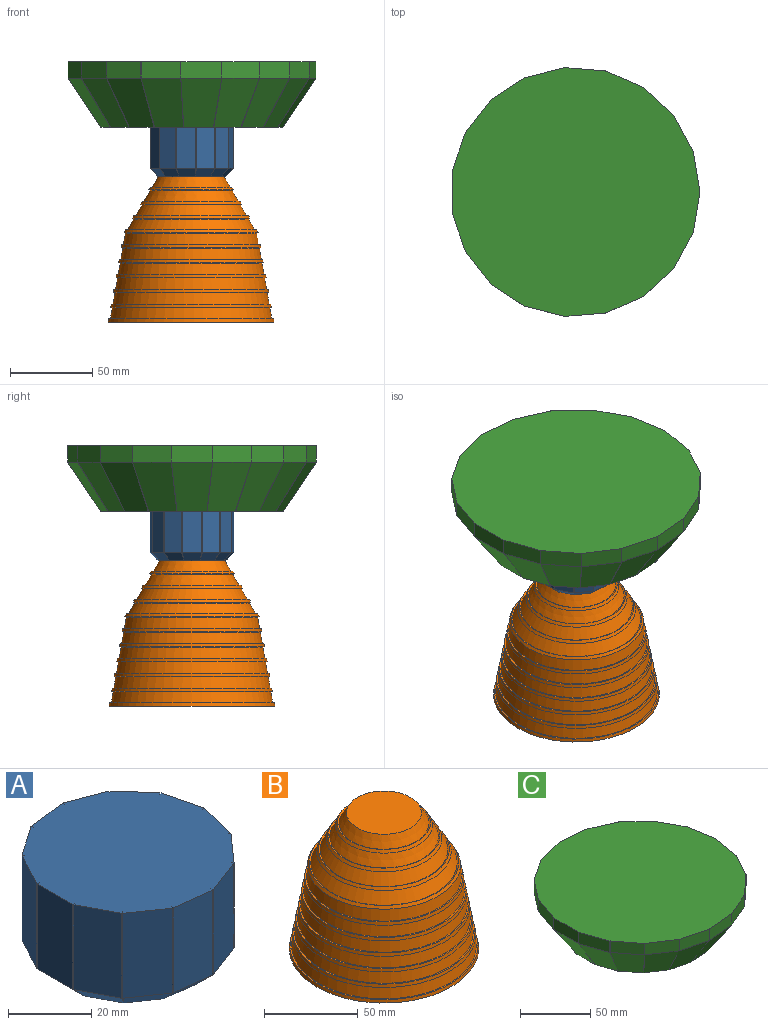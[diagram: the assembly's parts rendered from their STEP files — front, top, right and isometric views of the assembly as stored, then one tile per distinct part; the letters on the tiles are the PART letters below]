
ASSEMBLY  parts=3 mates=2
PART A: 132 faces, bbox 50.7x51.1x30 mm
  f0: plane 12x5mm, normal (-0.71,0,-0.71), area 77.3mm2, adj f2,f5,f8,f9,f128,f131
  f1: plane 0.23x0.23mm, normal (-0.71,0,-0.71), area 0mm2, adj f3,f5,f129
  f2: plane 4.77x4.77mm, normal (0,-0.98,-0.21), area 1.6mm2, adj f0,f4,f119
  f3: plane 0.23x0.23mm, normal (0,0.98,-0.21), area 0mm2, adj f1,f5,f127
  f4: plane 25x0.66mm, normal (0,-1,0), area 16.4mm2, adj f2,f9,f10,f117
  f5: plane 40.9x40.6mm, normal (0,0,-1), area 1281.7mm2, adj f0,f1,f3,f6,f7,f12,f13,f14
  f6: plane 0.23x0.23mm, normal (-0.71,0,-0.71), area 0mm2, adj f5,f7,f130
  f7: plane 0.23x0.23mm, normal (0,-0.98,-0.21), area 0mm2, adj f5,f6,f124
  f8: plane 4.77x4.77mm, normal (0,0.98,-0.21), area 1.6mm2, adj f0,f11,f126
  f9: plane 25x12mm, normal (-1,0,0), area 300mm2, adj f0,f4,f10,f11
  f10: plane 51.08x50.71mm, normal (0,0,1), area 2001.2mm2, adj f4,f9,f11,f16,f20,f21,f26,f30
  f11: plane 25x0.66mm, normal (0,1,0), area 16.4mm2, adj f8,f9,f10,f125
  f12: plane 0.23x0.17mm, normal (-0.8,0.56,-0.21), area 0mm2, adj f5,f13,f124
  f13: plane 0.23x0.17mm, normal (-0.4,-0.58,-0.71), area 0mm2, adj f5,f12,f121
  f14: plane 11.83x10.32mm, normal (-0.4,-0.58,-0.71), area 77.3mm2, adj f5,f15,f19,f20,f116,f120
  f15: plane 4.77x4.51mm, normal (0.8,-0.56,-0.21), area 1.6mm2, adj f14,f16,f109
  f16: plane 25x0.54mm, normal (0.82,-0.57,0), area 16.4mm2, adj f10,f15,f20,f107
  f17: plane 0.23x0.22mm, normal (-0.4,-0.58,-0.71), area 0mm2, adj f5,f18,f115
  f18: plane 0.23x0.22mm, normal (0.8,-0.56,-0.21), area 0mm2, adj f5,f17,f114
  f19: plane 4.77x3.55mm, normal (-0.8,0.56,-0.21), area 1.6mm2, adj f14,f21,f123
  f20: plane 25x9.88mm, normal (-0.57,-0.82,0), area 300mm2, adj f10,f14,f16,f21
  f21: plane 25x0.54mm, normal (-0.82,0.57,0), area 16.4mm2, adj f10,f19,f20,f122
  f22: plane 0.23x0.23mm, normal (-0.91,-0.35,-0.21), area 0mm2, adj f5,f23,f114
  f23: plane 0.23x0.23mm, normal (0.25,-0.66,-0.71), area 0mm2, adj f5,f22,f111
  f24: plane 11.98x8.55mm, normal (0.25,-0.66,-0.71), area 77.3mm2, adj f5,f25,f29,f30,f106,f110
  f25: plane 4.77x4.1mm, normal (0.91,0.35,-0.21), area 1.6mm2, adj f24,f26,f99
  f26: plane 25x0.61mm, normal (0.94,0.35,0), area 16.4mm2, adj f10,f25,f30,f97
  f27: plane 0.23x0.19mm, normal (0.25,-0.66,-0.71), area 0mm2, adj f5,f28,f105
  f28: plane 0.23x0.2mm, normal (0.91,0.35,-0.21), area 0mm2, adj f5,f27,f104
  f29: plane 4.82x4.77mm, normal (-0.91,-0.35,-0.21), area 1.6mm2, adj f24,f31,f113
  f30: plane 25x11.22mm, normal (0.35,-0.94,0), area 300mm2, adj f10,f24,f26,f31
  f31: plane 25x0.61mm, normal (-0.94,-0.35,0), area 16.4mm2, adj f10,f29,f30,f112
  f32: plane 0.23x0.21mm, normal (-0.23,-0.95,-0.21), area 0mm2, adj f5,f33,f104
  f33: plane 0.23x0.21mm, normal (0.69,-0.17,-0.71), area 0mm2, adj f5,f32,f101
  f34: plane 11.81x7.47mm, normal (0.69,-0.17,-0.71), area 77.3mm2, adj f5,f35,f39,f40,f96,f100
  f35: plane 4.88x4.77mm, normal (0.23,0.95,-0.21), area 1.6mm2, adj f34,f36,f89
  f36: plane 25x0.64mm, normal (0.24,0.97,0), area 16.4mm2, adj f10,f35,f40,f87
  f37: plane 0.23x0.23mm, normal (0.69,-0.17,-0.71), area 0mm2, adj f5,f38,f95
  f38: plane 0.23x0.23mm, normal (0.23,0.95,-0.21), area 0mm2, adj f5,f37,f94
  f39: plane 4.77x4.39mm, normal (-0.23,-0.95,-0.21), area 1.6mm2, adj f34,f41,f103
  f40: plane 25x11.65mm, normal (0.97,-0.24,0), area 300mm2, adj f10,f34,f36,f41
  f41: plane 25x0.64mm, normal (-0.24,-0.97,0), area 16.4mm2, adj f10,f39,f40,f102
  f42: plane 0.23x0.2mm, normal (0.65,-0.73,-0.21), area 0mm2, adj f5,f43,f94
  f43: plane 0.23x0.21mm, normal (0.53,0.47,-0.71), area 0mm2, adj f5,f42,f91
  f44: plane 11.49x10.98mm, normal (0.53,0.47,-0.71), area 77.3mm2, adj f5,f45,f49,f50,f86,f90
  f45: plane 4.77x3.93mm, normal (-0.65,0.73,-0.21), area 1.6mm2, adj f44,f46,f79
  f46: plane 25x0.49mm, normal (-0.66,0.75,0), area 16.4mm2, adj f10,f45,f50,f77
  f47: plane 0.23x0.19mm, normal (0.53,0.47,-0.71), area 0mm2, adj f5,f48,f85
  f48: plane 0.23x0.19mm, normal (-0.65,0.73,-0.21), area 0mm2, adj f5,f47,f84
  f49: plane 4.77x4.25mm, normal (0.65,-0.73,-0.21), area 1.6mm2, adj f44,f51,f93
  f50: plane 25x8.98mm, normal (0.75,0.66,0), area 300mm2, adj f10,f44,f46,f51
  f51: plane 25x0.49mm, normal (0.66,-0.75,0), area 16.4mm2, adj f10,f49,f50,f92
  f52: plane 0.23x0.23mm, normal (0.97,0.12,-0.21), area 0mm2, adj f5,f53,f84
  f53: plane 0.23x0.23mm, normal (-0.09,0.7,-0.71), area 0mm2, adj f5,f52,f81
  f54: plane 11.91x6.28mm, normal (-0.09,0.7,-0.71), area 77.3mm2, adj f5,f55,f59,f60,f76,f80
  f55: plane 4.77x4.62mm, normal (-0.97,-0.12,-0.21), area 1.6mm2, adj f54,f56,f69
  f56: plane 25x0.65mm, normal (-0.99,-0.12,0), area 16.4mm2, adj f10,f55,f60,f67
  f57: plane 0.23x0.22mm, normal (-0.09,0.7,-0.71), area 0mm2, adj f5,f58,f75
  f58: plane 0.23x0.22mm, normal (-0.97,-0.12,-0.21), area 0mm2, adj f5,f57,f74
  f59: plane 4.86x4.77mm, normal (0.97,0.12,-0.21), area 1.6mm2, adj f54,f61,f83
  f60: plane 25x11.91mm, normal (-0.12,0.99,0), area 300mm2, adj f10,f54,f56,f61
  f61: plane 25x0.65mm, normal (0.99,0.12,0), area 16.4mm2, adj f10,f59,f60,f82
  f62: plane 0.23x0.18mm, normal (0.45,0.87,-0.21), area 0mm2, adj f5,f63,f74
  f63: plane 0.23x0.18mm, normal (-0.63,0.33,-0.71), area 0mm2, adj f5,f62,f71
  f64: plane 4.77x3.76mm, normal (0.45,0.87,-0.21), area 1.6mm2, adj f66,f73,f127
  f65: plane 25x10.63mm, normal (-0.89,0.46,0), area 300mm2, adj f10,f66,f125,f127
  f66: plane 25x0.58mm, normal (0.46,0.89,0), area 16.4mm2, adj f10,f64,f65,f72
  f67: plane 25x0.54mm, normal (0.82,0.57,0), area 16.4mm2, adj f10,f56,f68,f69
  f68: plane 25x9.88mm, normal (-0.57,0.82,0), area 300mm2, adj f10,f67,f72,f74
  f69: plane 4.77x4.51mm, normal (0.8,0.56,-0.21), area 1.6mm2, adj f55,f67,f74
  f70: plane 0.23x0.17mm, normal (-0.8,-0.56,-0.21), area 0mm2, adj f5,f71,f127
  f71: plane 0.23x0.17mm, normal (-0.4,0.58,-0.71), area 0mm2, adj f5,f63,f70
  f72: plane 25x0.54mm, normal (-0.82,-0.57,0), area 16.4mm2, adj f10,f66,f68,f73
  f73: plane 4.77x3.55mm, normal (-0.8,-0.56,-0.21), area 1.6mm2, adj f64,f72,f74
  f74: plane 11.83x10.32mm, normal (-0.4,0.58,-0.71), area 77.3mm2, adj f5,f58,f62,f68,f69,f73
  f75: plane 0.23x0.22mm, normal (-0.4,0.58,-0.71), area 0mm2, adj f5,f57,f76
  f76: plane 0.23x0.22mm, normal (0.8,0.56,-0.21), area 0mm2, adj f5,f54,f75
  f77: plane 25x0.61mm, normal (0.94,-0.35,0), area 16.4mm2, adj f10,f46,f78,f79
  f78: plane 25x11.22mm, normal (0.35,0.94,0), area 300mm2, adj f10,f77,f82,f84
  f79: plane 4.77x4.1mm, normal (0.91,-0.35,-0.21), area 1.6mm2, adj f45,f77,f84
  f80: plane 0.23x0.23mm, normal (-0.91,0.35,-0.21), area 0mm2, adj f5,f54,f81
  f81: plane 0.23x0.23mm, normal (0.25,0.66,-0.71), area 0mm2, adj f5,f53,f80
  f82: plane 25x0.61mm, normal (-0.94,0.35,0), area 16.4mm2, adj f10,f61,f78,f83
  f83: plane 4.82x4.77mm, normal (-0.91,0.35,-0.21), area 1.6mm2, adj f59,f82,f84
  f84: plane 11.98x8.55mm, normal (0.25,0.66,-0.71), area 77.3mm2, adj f5,f48,f52,f78,f79,f83
  f85: plane 0.23x0.19mm, normal (0.25,0.66,-0.71), area 0mm2, adj f5,f47,f86
  f86: plane 0.23x0.2mm, normal (0.91,-0.35,-0.21), area 0mm2, adj f5,f44,f85
  f87: plane 25x0.64mm, normal (0.24,-0.97,0), area 16.4mm2, adj f10,f36,f88,f89
  f88: plane 25x11.65mm, normal (0.97,0.24,0), area 300mm2, adj f10,f87,f92,f94
  f89: plane 4.88x4.77mm, normal (0.23,-0.95,-0.21), area 1.6mm2, adj f35,f87,f94
  f90: plane 0.23x0.21mm, normal (-0.23,0.95,-0.21), area 0mm2, adj f5,f44,f91
  f91: plane 0.23x0.21mm, normal (0.69,0.17,-0.71), area 0mm2, adj f5,f43,f90
  f92: plane 25x0.64mm, normal (-0.24,0.97,0), area 16.4mm2, adj f10,f51,f88,f93
  f93: plane 4.77x4.39mm, normal (-0.23,0.95,-0.21), area 1.6mm2, adj f49,f92,f94
  f94: plane 11.81x7.47mm, normal (0.69,0.17,-0.71), area 77.3mm2, adj f5,f38,f42,f88,f89,f93
  f95: plane 0.23x0.23mm, normal (0.69,0.17,-0.71), area 0mm2, adj f5,f37,f96
  f96: plane 0.23x0.23mm, normal (0.23,-0.95,-0.21), area 0mm2, adj f5,f34,f95
  f97: plane 25x0.49mm, normal (-0.66,-0.75,0), area 16.4mm2, adj f10,f26,f98,f99
  f98: plane 25x8.98mm, normal (0.75,-0.66,0), area 300mm2, adj f10,f97,f102,f104
  f99: plane 4.77x3.93mm, normal (-0.65,-0.73,-0.21), area 1.6mm2, adj f25,f97,f104
  f100: plane 0.23x0.2mm, normal (0.65,0.73,-0.21), area 0mm2, adj f5,f34,f101
  f101: plane 0.23x0.21mm, normal (0.53,-0.47,-0.71), area 0mm2, adj f5,f33,f100
  f102: plane 25x0.49mm, normal (0.66,0.75,0), area 16.4mm2, adj f10,f41,f98,f103
  f103: plane 4.77x4.25mm, normal (0.65,0.73,-0.21), area 1.6mm2, adj f39,f102,f104
  f104: plane 11.49x10.98mm, normal (0.53,-0.47,-0.71), area 77.3mm2, adj f5,f28,f32,f98,f99,f103
  f105: plane 0.23x0.19mm, normal (0.53,-0.47,-0.71), area 0mm2, adj f5,f27,f106
  f106: plane 0.23x0.19mm, normal (-0.65,-0.73,-0.21), area 0mm2, adj f5,f24,f105
  f107: plane 25x0.65mm, normal (-0.99,0.12,0), area 16.4mm2, adj f10,f16,f108,f109
  f108: plane 25x11.91mm, normal (-0.12,-0.99,0), area 300mm2, adj f10,f107,f112,f114
  f109: plane 4.77x4.62mm, normal (-0.97,0.12,-0.21), area 1.6mm2, adj f15,f107,f114
  f110: plane 0.23x0.23mm, normal (0.97,-0.12,-0.21), area 0mm2, adj f5,f24,f111
  f111: plane 0.23x0.23mm, normal (-0.09,-0.7,-0.71), area 0mm2, adj f5,f23,f110
  f112: plane 25x0.65mm, normal (0.99,-0.12,0), area 16.4mm2, adj f10,f31,f108,f113
  f113: plane 4.86x4.77mm, normal (0.97,-0.12,-0.21), area 1.6mm2, adj f29,f112,f114
  f114: plane 11.91x6.28mm, normal (-0.09,-0.7,-0.71), area 77.3mm2, adj f5,f18,f22,f108,f109,f113
  f115: plane 0.23x0.22mm, normal (-0.09,-0.7,-0.71), area 0mm2, adj f5,f17,f116
  f116: plane 0.23x0.22mm, normal (-0.97,0.12,-0.21), area 0mm2, adj f5,f14,f115
  f117: plane 25x0.58mm, normal (-0.46,0.89,0), area 16.4mm2, adj f4,f10,f118,f119
  f118: plane 25x10.63mm, normal (-0.89,-0.46,0), area 300mm2, adj f10,f117,f122,f124
  f119: plane 4.77x4.7mm, normal (-0.45,0.87,-0.21), area 1.6mm2, adj f2,f117,f124
  f120: plane 0.23x0.18mm, normal (0.45,-0.87,-0.21), area 0mm2, adj f5,f14,f121
  f121: plane 0.23x0.18mm, normal (-0.63,-0.33,-0.71), area 0mm2, adj f5,f13,f120
  f122: plane 25x0.58mm, normal (0.46,-0.89,0), area 16.4mm2, adj f10,f21,f118,f123
  f123: plane 4.77x3.76mm, normal (0.45,-0.87,-0.21), area 1.6mm2, adj f19,f122,f124
  f124: plane 11.99x9.5mm, normal (-0.63,-0.33,-0.71), area 77.3mm2, adj f5,f7,f12,f118,f119,f123
  f125: plane 25x0.58mm, normal (-0.46,-0.89,0), area 16.4mm2, adj f10,f11,f65,f126
  f126: plane 4.77x4.7mm, normal (-0.45,-0.87,-0.21), area 1.6mm2, adj f8,f125,f127
  f127: plane 11.99x9.5mm, normal (-0.63,0.33,-0.71), area 77.3mm2, adj f3,f5,f64,f65,f70,f126
  f128: plane 0.23x0.23mm, normal (-0.45,-0.87,-0.21), area 0mm2, adj f0,f5,f129
  f129: plane 0.23x0.23mm, normal (-0.63,0.33,-0.71), area 0mm2, adj f1,f5,f128
  f130: plane 0.23x0.23mm, normal (-0.63,-0.33,-0.71), area 0mm2, adj f5,f6,f131
  f131: plane 0.23x0.23mm, normal (-0.45,0.87,-0.21), area 0mm2, adj f0,f5,f130
PART B: 45 faces, bbox 101.1x101.1x88.8 mm
  f0: cone r=47.96mm half-angle=80deg, axis (0,0,1), area 304.4mm2, adj f1,f44
  f1: cone r=49.2mm half-angle=10deg, axis (0,0,-1), area 2187.6mm2, adj f0,f2
  f2: cone r=49.2mm half-angle=80deg, axis (0,0,1), area 312.2mm2, adj f1,f3
  f3: cone r=50.54mm half-angle=10deg, axis (0,0,-1), area 632.9mm2, adj f2,f4
  f4: cone r=49.55mm half-angle=80deg, axis (0,0,1), area 314.4mm2, adj f3,f5
  f5: plane 99.1x99.1mm, normal (0,0,-1), area 1499.7mm2, adj f4,f6
  f6: cone r=44.47mm half-angle=10deg, axis (0,0,-1), area 13330.1mm2, adj f5,f7
  f7: cone r=17.11mm half-angle=30deg, axis (0,0,-1), area 5957.9mm2, adj f6,f8
  f8: plane 34.23x34.23mm, normal (0,0,-1), area 920.1mm2, adj f7
  f9: plane 40x40mm, normal (0,0,1), area 1256.6mm2, adj f10
  f10: cone r=24mm half-angle=30deg, axis (0,0,-1), area 1105.8mm2, adj f9,f11
  f11: cone r=24mm half-angle=60deg, axis (0,0,1), area 153.5mm2, adj f10,f12
  f12: cone r=25.87mm half-angle=30deg, axis (0,0,-1), area 318.8mm2, adj f11,f13
  f13: cone r=25mm half-angle=60deg, axis (0,0,1), area 159.8mm2, adj f12,f14
  f14: cone r=29mm half-angle=30deg, axis (0,0,-1), area 1357.2mm2, adj f13,f15
  f15: cone r=29mm half-angle=60deg, axis (0,0,1), area 184.9mm2, adj f14,f16
  f16: cone r=30.87mm half-angle=30deg, axis (0,0,-1), area 381.6mm2, adj f15,f17
  f17: cone r=30mm half-angle=60deg, axis (0,0,1), area 191.2mm2, adj f16,f18
  f18: cone r=34mm half-angle=30deg, axis (0,0,-1), area 1608.5mm2, adj f17,f19
  f19: cone r=34mm half-angle=60deg, axis (0,0,1), area 216.3mm2, adj f18,f20
  f20: cone r=35.87mm half-angle=30deg, axis (0,0,-1), area 444.4mm2, adj f19,f21
  f21: cone r=35mm half-angle=60deg, axis (0,0,1), area 222.6mm2, adj f20,f22
  f22: cone r=39mm half-angle=30deg, axis (0,0,-1), area 1859.8mm2, adj f21,f23
  f23: cone r=39mm half-angle=60deg, axis (0,0,1), area 247.8mm2, adj f22,f24
  f24: cone r=40.87mm half-angle=30deg, axis (0,0,-1), area 507.3mm2, adj f23,f25
  f25: cone r=40mm half-angle=60deg, axis (0,0,1), area 254mm2, adj f24,f26
  f26: cone r=41.24mm half-angle=10deg, axis (0,0,-1), area 1829.2mm2, adj f25,f27
  f27: cone r=41.24mm half-angle=80deg, axis (0,0,1), area 262.2mm2, adj f26,f28
  f28: cone r=42.58mm half-angle=10deg, axis (0,0,-1), area 532.9mm2, adj f27,f29
  f29: cone r=41.59mm half-angle=80deg, axis (0,0,1), area 264.4mm2, adj f28,f30
  f30: cone r=42.84mm half-angle=10deg, axis (0,0,-1), area 1900.9mm2, adj f29,f31
  f31: cone r=42.84mm half-angle=80deg, axis (0,0,1), area 272.2mm2, adj f30,f32
  f32: cone r=44.17mm half-angle=10deg, axis (0,0,-1), area 552.9mm2, adj f31,f33
  f33: cone r=43.18mm half-angle=80deg, axis (0,0,1), area 274.4mm2, adj f32,f34
  f34: cone r=44.43mm half-angle=10deg, axis (0,0,-1), area 1972.6mm2, adj f33,f35
  f35: cone r=44.43mm half-angle=80deg, axis (0,0,1), area 282.2mm2, adj f34,f36
  f36: cone r=45.76mm half-angle=10deg, axis (0,0,-1), area 572.9mm2, adj f35,f37
  f37: cone r=44.78mm half-angle=80deg, axis (0,0,1), area 284.4mm2, adj f36,f38
  f38: cone r=46.02mm half-angle=10deg, axis (0,0,-1), area 2044.2mm2, adj f37,f39
  f39: cone r=46.02mm half-angle=80deg, axis (0,0,1), area 292.2mm2, adj f38,f40
  f40: cone r=47.35mm half-angle=10deg, axis (0,0,-1), area 592.9mm2, adj f39,f41
  f41: cone r=46.37mm half-angle=80deg, axis (0,0,1), area 294.4mm2, adj f40,f42
  f42: cone r=47.61mm half-angle=10deg, axis (0,0,-1), area 2115.9mm2, adj f41,f43
  f43: cone r=47.61mm half-angle=80deg, axis (0,0,1), area 302.2mm2, adj f42,f44
  f44: cone r=48.94mm half-angle=10deg, axis (0,0,-1), area 612.9mm2, adj f0,f43
PART C: 116 faces, bbox 151x151.6x40 mm
  f0: plane 30x20.58mm, normal (0,-0.99,-0.11), area 10.1mm2, adj f1,f2,f3,f13
  f1: plane 10x0.09mm, normal (0,-1,0), area 0.9mm2, adj f0,f5,f6,f15
  f2: plane 111.12x110.74mm, normal (0,0,-1), area 9589.8mm2, adj f0,f3,f4,f8,f10,f12,f13,f16
  f3: plane 30x25mm, normal (-0.83,0,-0.55), area 778.1mm2, adj f0,f2,f4,f6
  f4: plane 30x20.58mm, normal (0,0.99,-0.11), area 10.1mm2, adj f2,f3,f7,f8
  f5: plane 151.55x151.03mm, normal (0,0,1), area 17834.3mm2, adj f1,f6,f7,f9,f11,f14,f15,f17
  f6: plane 25x10mm, normal (-1,0,0), area 250mm2, adj f1,f3,f5,f7
  f7: plane 10x0.09mm, normal (0,1,0), area 0.9mm2, adj f4,f5,f6,f9
  f8: plane 30x20.57mm, normal (-0.32,-0.94,-0.11), area 10.1mm2, adj f2,f4,f9,f112
  f9: plane 10x0.09mm, normal (-0.32,-0.95,0), area 0.9mm2, adj f5,f7,f8,f114
  f10: plane 30x18.35mm, normal (0.32,-0.94,-0.11), area 10.1mm2, adj f2,f11,f12,f19
  f11: plane 10x0.09mm, normal (0.32,-0.95,0), area 0.9mm2, adj f5,f10,f14,f21
  f12: plane 30x26.91mm, normal (-0.79,-0.27,-0.55), area 778.1mm2, adj f2,f10,f13,f14
  f13: plane 30x20.57mm, normal (-0.32,0.94,-0.11), area 10.1mm2, adj f0,f2,f12,f15
  f14: plane 23.65x10mm, normal (-0.95,-0.32,0), area 250mm2, adj f5,f11,f12,f15
  f15: plane 10x0.09mm, normal (-0.32,0.95,0), area 0.9mm2, adj f1,f5,f13,f14
  f16: plane 30x15.33mm, normal (0.61,-0.78,-0.11), area 10.1mm2, adj f2,f17,f18,f25
  f17: plane 10x0.07mm, normal (0.61,-0.79,0), area 0.9mm2, adj f5,f16,f20,f27
  f18: plane 30x29.32mm, normal (-0.66,-0.51,-0.55), area 778.1mm2, adj f2,f16,f19,f20
  f19: plane 30x18.34mm, normal (-0.61,0.78,-0.11), area 10.1mm2, adj f2,f10,f18,f21
  f20: plane 19.73x15.36mm, normal (-0.79,-0.61,0), area 250mm2, adj f5,f17,f18,f21
  f21: plane 10x0.07mm, normal (-0.61,0.79,0), area 0.9mm2, adj f5,f11,f19,f20
  f22: plane 30x19.09mm, normal (0.83,-0.54,-0.11), area 10.1mm2, adj f2,f23,f24,f31
  f23: plane 10x0.08mm, normal (0.84,-0.55,0), area 0.9mm2, adj f5,f22,f26,f33
  f24: plane 30x29.01mm, normal (-0.46,-0.7,-0.55), area 778.1mm2, adj f2,f22,f25,f26
  f25: plane 30x15.36mm, normal (-0.83,0.54,-0.11), area 10.1mm2, adj f2,f16,f24,f27
  f26: plane 20.93x13.67mm, normal (-0.55,-0.84,0), area 250mm2, adj f5,f23,f24,f27
  f27: plane 10x0.08mm, normal (-0.84,0.55,0), area 0.9mm2, adj f5,f17,f25,f26
  f28: plane 30x20.78mm, normal (0.96,-0.24,-0.11), area 10.1mm2, adj f2,f29,f30,f37
  f29: plane 10x0.09mm, normal (0.97,-0.25,0), area 0.9mm2, adj f5,f28,f32,f39
  f30: plane 30x25.83mm, normal (-0.2,-0.81,-0.55), area 778.1mm2, adj f2,f28,f31,f32
  f31: plane 30x19.11mm, normal (-0.96,0.24,-0.11), area 10.1mm2, adj f2,f22,f30,f33
  f32: plane 24.24x10mm, normal (-0.25,-0.97,0), area 250mm2, adj f5,f29,f30,f33
  f33: plane 10x0.09mm, normal (-0.97,0.25,0), area 0.9mm2, adj f5,f23,f31,f32
  f34: plane 30x20.22mm, normal (0.99,0.08,-0.11), area 10.1mm2, adj f2,f35,f36,f43
  f35: plane 10x0.09mm, normal (1,0.08,0), area 0.9mm2, adj f5,f34,f38,f45
  f36: plane 30x24.91mm, normal (0.07,-0.83,-0.55), area 778.1mm2, adj f2,f34,f37,f38
  f37: plane 30x20.79mm, normal (-0.99,-0.08,-0.11), area 10.1mm2, adj f2,f28,f36,f39
  f38: plane 24.91x10mm, normal (0.08,-1,0), area 250mm2, adj f5,f35,f36,f39
  f39: plane 10x0.09mm, normal (-1,-0.08,0), area 0.9mm2, adj f5,f29,f37,f38
  f40: plane 30x17.47mm, normal (0.91,0.4,-0.11), area 10.1mm2, adj f2,f41,f42,f49
  f41: plane 10x0.08mm, normal (0.92,0.4,0), area 0.9mm2, adj f5,f40,f44,f51
  f42: plane 30x27.8mm, normal (0.33,-0.76,-0.55), area 778.1mm2, adj f2,f40,f43,f44
  f43: plane 30x20.22mm, normal (-0.91,-0.4,-0.11), area 10.1mm2, adj f2,f34,f42,f45
  f44: plane 22.89x10.04mm, normal (0.4,-0.92,0), area 250mm2, adj f5,f41,f42,f45
  f45: plane 10x0.08mm, normal (-0.92,-0.4,0), area 0.9mm2, adj f5,f35,f43,f44
  f46: plane 30x16.45mm, normal (0.73,0.67,-0.11), area 10.1mm2, adj f2,f47,f48,f55
  f47: plane 10x0.07mm, normal (0.74,0.68,0), area 0.9mm2, adj f5,f46,f50,f57
  f48: plane 30x29.42mm, normal (0.56,-0.61,-0.55), area 778.1mm2, adj f2,f46,f49,f50
  f49: plane 30x17.45mm, normal (-0.73,-0.67,-0.11), area 10.1mm2, adj f2,f40,f48,f51
  f50: plane 18.39x16.93mm, normal (0.68,-0.74,0), area 250mm2, adj f5,f47,f48,f51
  f51: plane 10x0.07mm, normal (-0.74,-0.68,0), area 0.9mm2, adj f5,f41,f49,f50
  f52: plane 30x19.72mm, normal (0.47,0.87,-0.11), area 10.1mm2, adj f2,f53,f54,f61
  f53: plane 10x0.08mm, normal (0.48,0.88,0), area 0.9mm2, adj f5,f52,f56,f63
  f54: plane 30x28.5mm, normal (0.73,-0.4,-0.55), area 778.1mm2, adj f2,f52,f55,f56
  f55: plane 30x16.47mm, normal (-0.47,-0.87,-0.11), area 10.1mm2, adj f2,f46,f54,f57
  f56: plane 21.99x11.9mm, normal (0.88,-0.48,0), area 250mm2, adj f5,f53,f54,f57
  f57: plane 10x0.08mm, normal (-0.48,-0.88,0), area 0.9mm2, adj f5,f47,f55,f56
  f58: plane 30x20.86mm, normal (0.16,0.98,-0.11), area 10.1mm2, adj f2,f59,f60,f67
  f59: plane 10x0.09mm, normal (0.16,0.99,0), area 0.9mm2, adj f5,f58,f62,f69
  f60: plane 30x24.66mm, normal (0.82,-0.14,-0.55), area 778.1mm2, adj f2,f58,f61,f62
  f61: plane 30x19.73mm, normal (-0.16,-0.98,-0.11), area 10.1mm2, adj f2,f52,f60,f63
  f62: plane 24.66x10mm, normal (0.99,-0.16,0), area 250mm2, adj f5,f59,f60,f63
  f63: plane 10x0.09mm, normal (-0.16,-0.99,0), area 0.9mm2, adj f5,f53,f61,f62
  f64: plane 30x19.73mm, normal (-0.16,0.98,-0.11), area 10.1mm2, adj f2,f65,f66,f73
  f65: plane 10x0.09mm, normal (-0.16,0.99,0), area 0.9mm2, adj f5,f64,f68,f75
  f66: plane 30x24.66mm, normal (0.82,0.14,-0.55), area 778.1mm2, adj f2,f64,f67,f68
  f67: plane 30x20.86mm, normal (0.16,-0.98,-0.11), area 10.1mm2, adj f2,f58,f66,f69
  f68: plane 24.66x10mm, normal (0.99,0.16,0), area 250mm2, adj f5,f65,f66,f69
  f69: plane 10x0.09mm, normal (0.16,-0.99,0), area 0.9mm2, adj f5,f59,f67,f68
  f70: plane 30x16.47mm, normal (-0.47,0.87,-0.11), area 10.1mm2, adj f2,f71,f72,f79
  f71: plane 10x0.08mm, normal (-0.48,0.88,0), area 0.9mm2, adj f5,f70,f74,f81
  f72: plane 30x28.5mm, normal (0.73,0.4,-0.55), area 778.1mm2, adj f2,f70,f73,f74
  f73: plane 30x19.72mm, normal (0.47,-0.87,-0.11), area 10.1mm2, adj f2,f64,f72,f75
  f74: plane 21.99x11.9mm, normal (0.88,0.48,0), area 250mm2, adj f5,f71,f72,f75
  f75: plane 10x0.08mm, normal (0.48,-0.88,0), area 0.9mm2, adj f5,f65,f73,f74
  f76: plane 30x17.45mm, normal (-0.73,0.67,-0.11), area 10.1mm2, adj f2,f77,f78,f85
  f77: plane 10x0.07mm, normal (-0.74,0.68,0), area 0.9mm2, adj f5,f76,f80,f87
  f78: plane 30x29.42mm, normal (0.56,0.61,-0.55), area 778.1mm2, adj f2,f76,f79,f80
  f79: plane 30x16.45mm, normal (0.73,-0.67,-0.11), area 10.1mm2, adj f2,f70,f78,f81
  f80: plane 18.39x16.93mm, normal (0.68,0.74,0), area 250mm2, adj f5,f77,f78,f81
  f81: plane 10x0.07mm, normal (0.74,-0.68,0), area 0.9mm2, adj f5,f71,f79,f80
  f82: plane 30x20.22mm, normal (-0.91,0.4,-0.11), area 10.1mm2, adj f2,f83,f84,f91
  f83: plane 10x0.08mm, normal (-0.92,0.4,0), area 0.9mm2, adj f5,f82,f86,f93
  f84: plane 30x27.8mm, normal (0.33,0.76,-0.55), area 778.1mm2, adj f2,f82,f85,f86
  f85: plane 30x17.47mm, normal (0.91,-0.4,-0.11), area 10.1mm2, adj f2,f76,f84,f87
  f86: plane 22.89x10.04mm, normal (0.4,0.92,0), area 250mm2, adj f5,f83,f84,f87
  f87: plane 10x0.08mm, normal (0.92,-0.4,0), area 0.9mm2, adj f5,f77,f85,f86
  f88: plane 30x20.79mm, normal (-0.99,0.08,-0.11), area 10.1mm2, adj f2,f89,f90,f97
  f89: plane 10x0.09mm, normal (-1,0.08,0), area 0.9mm2, adj f5,f88,f92,f99
  f90: plane 30x24.91mm, normal (0.07,0.83,-0.55), area 778.1mm2, adj f2,f88,f91,f92
  f91: plane 30x20.22mm, normal (0.99,-0.08,-0.11), area 10.1mm2, adj f2,f82,f90,f93
  f92: plane 24.91x10mm, normal (0.08,1,0), area 250mm2, adj f5,f89,f90,f93
  f93: plane 10x0.09mm, normal (1,-0.08,0), area 0.9mm2, adj f5,f83,f91,f92
  f94: plane 30x19.11mm, normal (-0.96,-0.24,-0.11), area 10.1mm2, adj f2,f95,f96,f103
  f95: plane 10x0.09mm, normal (-0.97,-0.25,0), area 0.9mm2, adj f5,f94,f98,f105
  f96: plane 30x25.83mm, normal (-0.2,0.81,-0.55), area 778.1mm2, adj f2,f94,f97,f98
  f97: plane 30x20.78mm, normal (0.96,0.24,-0.11), area 10.1mm2, adj f2,f88,f96,f99
  f98: plane 24.24x10mm, normal (-0.25,0.97,0), area 250mm2, adj f5,f95,f96,f99
  f99: plane 10x0.09mm, normal (0.97,0.25,0), area 0.9mm2, adj f5,f89,f97,f98
  f100: plane 30x15.36mm, normal (-0.83,-0.54,-0.11), area 10.1mm2, adj f2,f101,f102,f109
  f101: plane 10x0.08mm, normal (-0.84,-0.55,0), area 0.9mm2, adj f5,f100,f104,f111
  f102: plane 30x29.01mm, normal (-0.46,0.7,-0.55), area 778.1mm2, adj f2,f100,f103,f104
  f103: plane 30x19.09mm, normal (0.83,0.54,-0.11), area 10.1mm2, adj f2,f94,f102,f105
  f104: plane 20.93x13.67mm, normal (-0.55,0.84,0), area 250mm2, adj f5,f101,f102,f105
  f105: plane 10x0.08mm, normal (0.84,0.55,0), area 0.9mm2, adj f5,f95,f103,f104
  f106: plane 30x18.34mm, normal (-0.61,-0.78,-0.11), area 10.1mm2, adj f2,f107,f108,f113
  f107: plane 10x0.07mm, normal (-0.61,-0.79,0), area 0.9mm2, adj f5,f106,f110,f115
  f108: plane 30x29.32mm, normal (-0.66,0.51,-0.55), area 778.1mm2, adj f2,f106,f109,f110
  f109: plane 30x15.33mm, normal (0.61,0.78,-0.11), area 10.1mm2, adj f2,f100,f108,f111
  f110: plane 19.73x15.36mm, normal (-0.79,0.61,0), area 250mm2, adj f5,f107,f108,f111
  f111: plane 10x0.07mm, normal (0.61,0.79,0), area 0.9mm2, adj f5,f101,f109,f110
  f112: plane 30x26.91mm, normal (-0.79,0.27,-0.55), area 778.1mm2, adj f2,f8,f113,f114
  f113: plane 30x18.35mm, normal (0.32,0.94,-0.11), area 10.1mm2, adj f2,f106,f112,f115
  f114: plane 23.65x10mm, normal (-0.95,0.32,0), area 250mm2, adj f5,f9,f112,f115
  f115: plane 10x0.09mm, normal (0.32,0.95,0), area 0.9mm2, adj f5,f107,f113,f114
PLACE A t=(0.12,0.09,-27.39)mm fixed
PLACE B t=(0.12,0.09,-27.39)mm
PLACE C t=(0.12,0.09,-27.39)mm
MATE ball A.f5 <-> B.f0  axis (0,0,-1) through (0.12,0.09,8.99)mm
MATE fastened C.f2 <-> A.f10  axis (0,0,-1) through (0.12,0.09,38.99)mm
